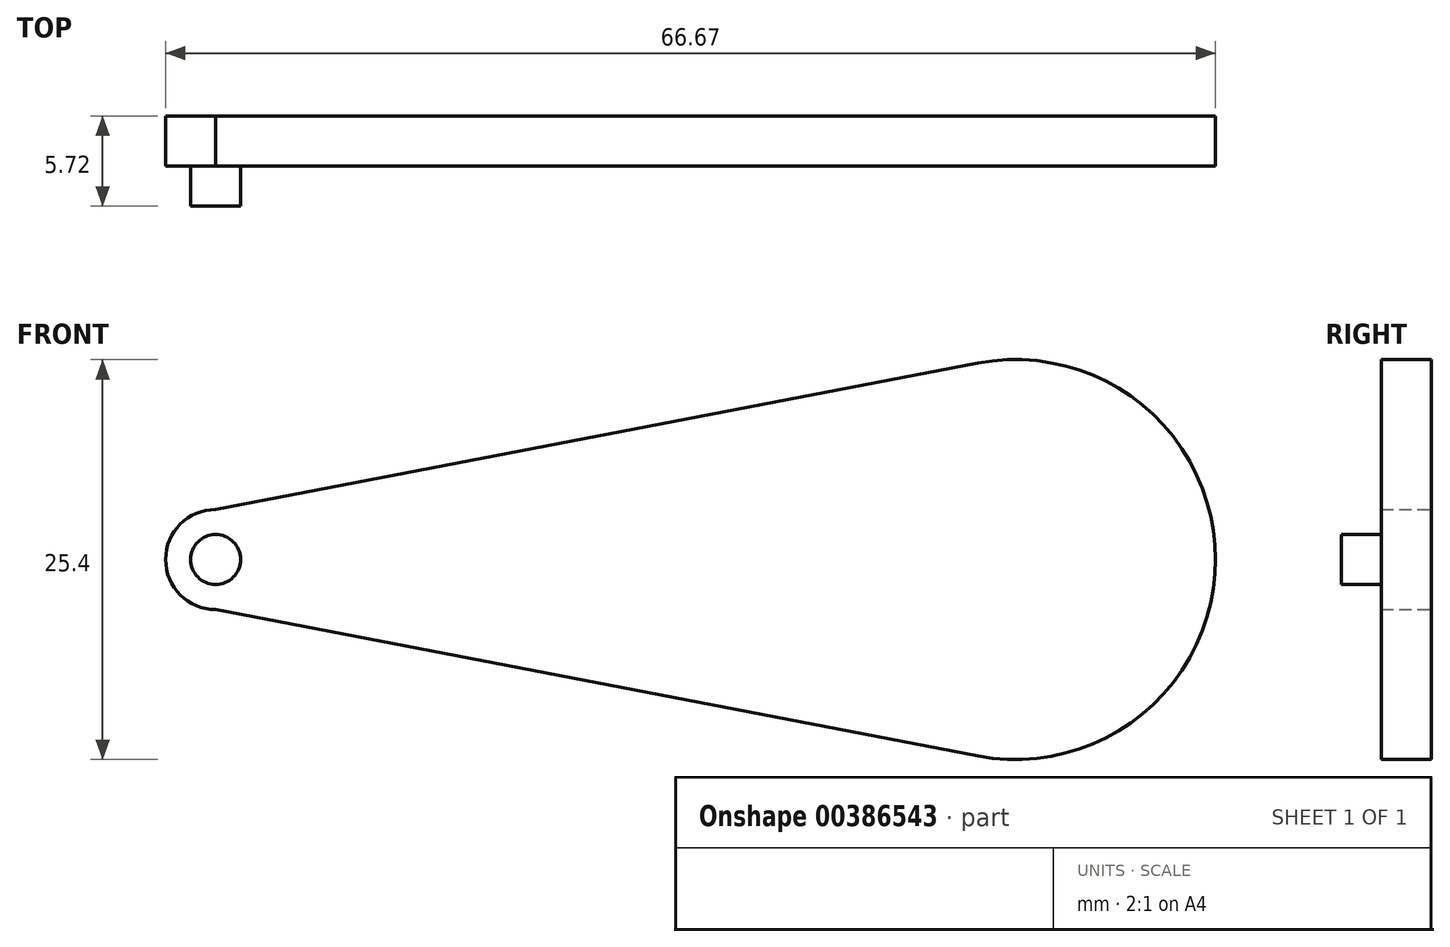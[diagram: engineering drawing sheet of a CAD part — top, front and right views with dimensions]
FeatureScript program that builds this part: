
annotation { "Feature Type Name" : "Feature", "Feature Type Description" : "" }
export const myFeature = defineFeature(function(context is Context, id is Id, definition is map)
    precondition{}
    {
        {
            var Q0;
            Q0=qCreatedBy(makeId("Front.planeOp"),FACE);
            var sketch = newSketch(context, id + "F0", { "sketchPlane" : qUnion([Q0])});
            skArc(sketch, "E0", {"start": v(-18.68, 3.18) * mm, "mid": v(-21.85, 0) * mm, "end": v(-18.68, -3.18) * mm});
            skArc(sketch, "E1", {"start": v(29.73, -12.47) * mm, "mid": v(44.82, 0) * mm, "end": v(29.73, 12.47) * mm});
            skLineSegment(sketch, "E2", {"start": v(-18.68, 3.17) * mm, "end": v(29.73, 12.47) * mm});
            skLineSegment(sketch, "E3", {"start": v(-18.68, -3.17) * mm, "end": v(29.73, -12.47) * mm});
            skCircle(sketch, "E4", {"center": v(-18.68, 0) * mm, "radius": 1.59 * mm});
            skSolve(sketch);
        }
        {
            var Q0;
            Q0 = qSketchRegion(id + "F0", true);
            extrude(context, id + "F1", {"entities" : qUnion([Q0]), "depth" : 3.17 * mm});
        }
        {
            var Q0;
            Q0=makeQuery(id+"F0.imprint","IMPRINT",FACE,{"disambiguationData":[TD([[makeQuery(id+"F0.imprint","IMPRINT",EDGE,{"derivedFrom":sQuery(id+"F0.wireOp",EDGE,"E4")}),1.0]])]});
            extrude(context, id + "F2", {"entities" : qUnion([Q0]), "operationType" : NewBodyOperationType.ADD, "depth" : 5.7 * mm});
        }
    });
